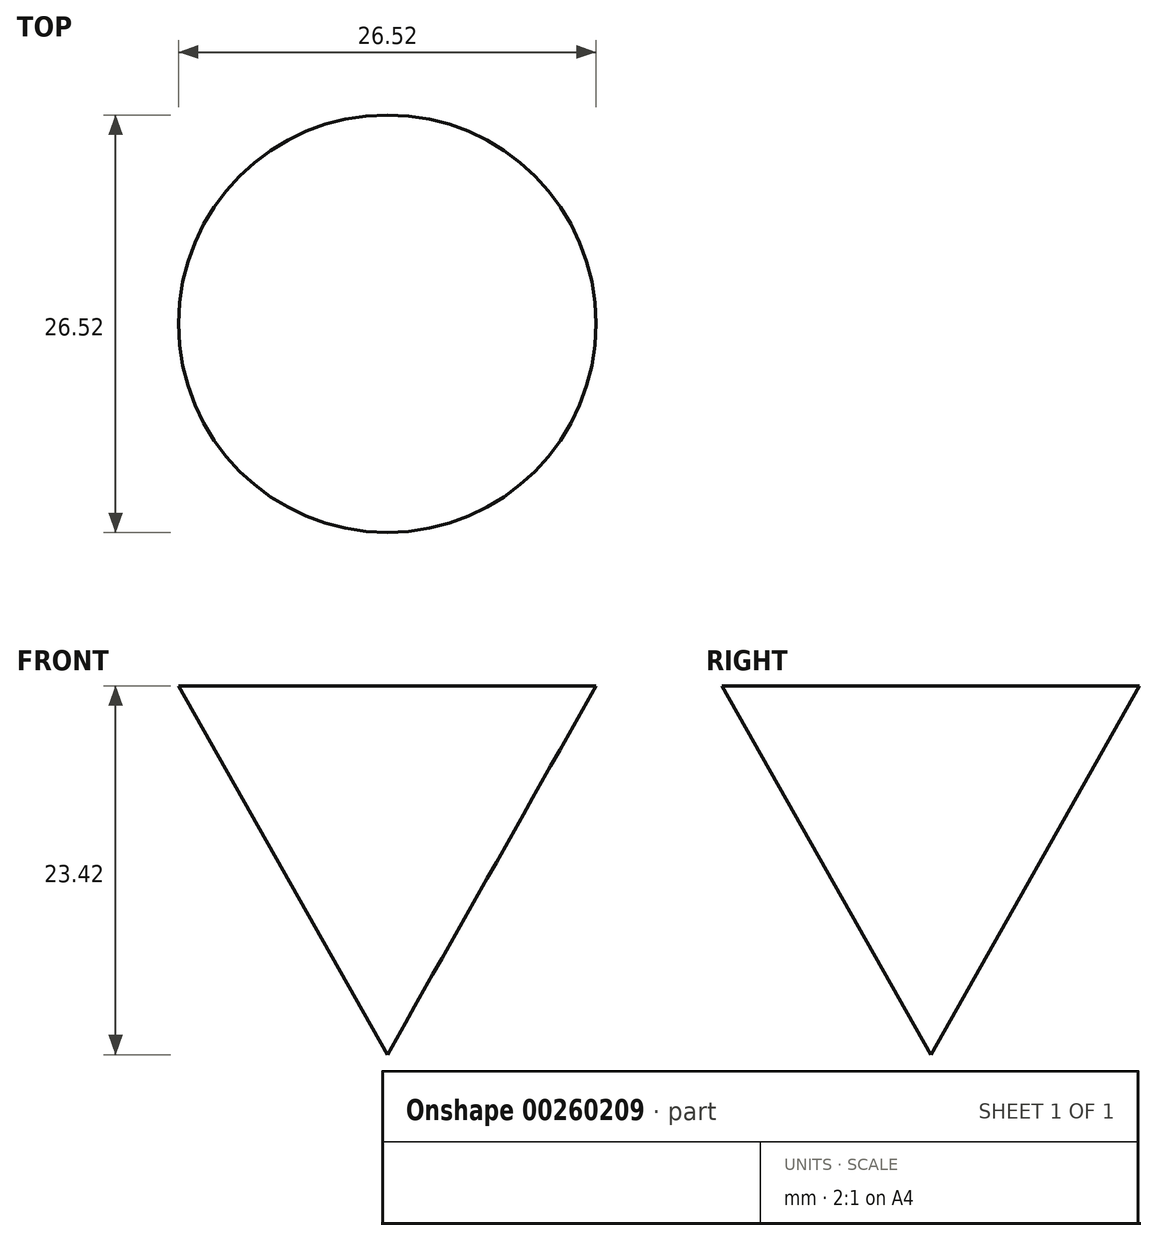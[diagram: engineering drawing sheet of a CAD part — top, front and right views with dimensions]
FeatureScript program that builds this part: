
annotation { "Feature Type Name" : "Feature", "Feature Type Description" : "" }
export const myFeature = defineFeature(function(context is Context, id is Id, definition is map)
    precondition{}
    {
        {
            var Q0;
            Q0=qCreatedBy(makeId("Front.planeOp"),FACE);
            var sketch = newSketch(context, id + "F0", { "sketchPlane" : qUnion([Q0])});
            skLineSegment(sketch, "E0", {"start": v(0, 17.97) * mm, "end": v(0, 33.3) * mm});
            skLineSegment(sketch, "E1", {"start": v(0, 33.3) * mm, "end": v(13.26, 56.72) * mm});
            skSolve(sketch);
        }
        {
            var Q0;
            Q0 = qSketchRegion(id + "F0", true);
            var Q1;
            Q1=sQuery(id+"F0.wireOp",EDGE,"E1");
            var Q2;
            Q2=sQuery(id+"F0.wireOp",EDGE,"E0");
            revolve(context, id + "F1", {"bodyType" : ToolBodyType.SURFACE, "entities" : qUnion([Q0]), "surfaceEntities" : qUnion([Q1]), "axis" : qUnion([Q2]), "revolveType" : RevolveType.FULL});
        }
    });
